# Revit family: TYCO-FPP-Zettler-MIM800 mini-input monitor module
name_source: partatom
category: Electrical Fixtures
revit_build: Autodesk Revit 2014 (Build: 20130308_1515(x64)
units: mm (PartAtom-declared; Revit-internal decimal feet)

## types (1)
- TYCO-FPP-Zettler-MIM800 mini-input monitor module
    Alarm State Current = 2.8mA
    Ambient Temperature = –25°C to +70°C
    COVER = Cap
    Description = The MIM800 or MIM801 Addressable Mini Input Module
supervises one circuit of voltage-free contacts, such as
outputs from extinguishing systems, ventilation controls,
etc., and transmits its state to the Tyco MX Control and
Indicating Equipment (CIE).
    Length = 48 mm
    Loop Voltage = 20V to 40Vdc
    Manufacturer = Tyco
    Max. MIM800 / Loop2 = 200/250
200/250
    Model = Zettler - 555.800.001
    PCB = PCB
    Quiescent Current = 275μA (typical)
    Relative Humidity = 10% to 95%
    Storage Temperature = –40°C to +80°C
    Thickness = 13 mm
    Type Comments = The MIM800 is a small MZX addressable module
designed for monitoring a single input circuit.
    URL = https://www.tycosafetyproducts-anz.com
    Weight = 22g
    Width = 57 mm

## geometry (parser evidence)
native form markers: Sweep x1
no freeform markers — native parametric forms only
